# Revit family: LOROWERK 01391-100X
name_source: partatom
category: Plumbing Fixtures
revit_build: Autodesk Revit 2017 (Build: 20160225_1515(x64)
units: mm (PartAtom-declared; Revit-internal decimal feet)

## family parameters
Always vertical = Yes
Cut with Voids When Loaded = No
Part Type = Normal
Room Calculation Point = No
Round Connector Dimension = Use Diameter
Shared = No
Work Plane-Based = No

## types (1)
- LOROWERK 01391-100X
    38.710.01.13 = seitlich
    38.710.01.5 = DN
    Abdichtvarianten = mit Klemmflansch
    Abflussstutzen Ausführung = waagerecht
    Ablaufanschluss = 1
    Art der Nenn-/ Betriebsspannung = nicht zutreffend
    BIM = https://media.stage.bim.site
    Bestellmenge (Multiplikator) Number = 1
    CONNECTOR0_DIAMETER_dZ_0r = 100 mm  [stored 0.328084 ft]
    CONNECTOR0_dZ_00 = 47 mm
    CONNECTOR0_dZ_01 = 47 mm
    CONNECTOR0_ref_dZ = 47 mm
    CONNECTOR1_DIAMETER_dNBN0_0r = 100 mm  [stored 0.328084 ft]
    CONNECTOR1_dNBN0_00 = 216 mm
    CONNECTOR1_dNBN0_01 = 290 mm
    CONNECTOR1_ref_dNBN0 = 216 mm
    CONNECTOR1_ref_dNBN1 = 49 mm
    DATANORM = 01391.100X
    Description = LORO-RAINSTAR Attikaabläufe, Serie 88, Attika-Distant, ohne Aufkantung
    Elektrischer Anschluss = nein
    Feuerwiderstandsklasse = keine Feuerwiderstandsklasse
    Feuerwiderstandsklasse nachrüstbar = nein
    GTIN = 4038088074206
    Gehäuseanschlussarten = Ablauf punktförmig
    Geruchsverschluss = ohne Geruchsverschluss
    HAN = 01391.100X
    HeinzeBIM = https://www.heinze.de
    Heizung = ohne Heizung
    Kommentar = Serie 88, Attika-Distant, ohne Aufkantung
    Manufacturer = LOROWERK K.H. Vahlbrauk GmbH & Co. KG
    Nenndruck Text = 422
    Nenndrucksystem Text = 270
    Nennweitensystem Text = PN
    Potenzialausgleich (Erdungsanschluss)   vorhanden = ja
    Produktbezeichnung Text = LORO-RAINSTAR 88 Attikanotablauf, ohne Aufkant., Edelst., Klemmfl., Freispiegel, DN100
    Produktklassifikation = Attikaablauf
    Produktname Text = LORO-RAINSTAR 88 Attikanotablauf, ohne Aufkant., Edelst., Klemmfl., Freispiegel, DN100
    Produktvideo = https://media.stage.bim.site
    Typ = Notablauf
    Type Name = LORO-RAINSTAR 88 Attikanotablauf, ohne Aufkant., Edelst., Klemmfl., Freispiegel, DN100
    VDIBSN = 0020090000020010000010020010010000000030020000001000000001
    Werkstoff des Ablaufkörpers = nicht rostender Stahl
    Wärmedämmung = ohne Wärmedämmung

note: [stored X ft] marks values corroborated as IEEE doubles in the binary element streams (Revit-internal decimal feet)

## geometry (parser evidence)
native form markers: Blend x2
no freeform markers — native parametric forms only
